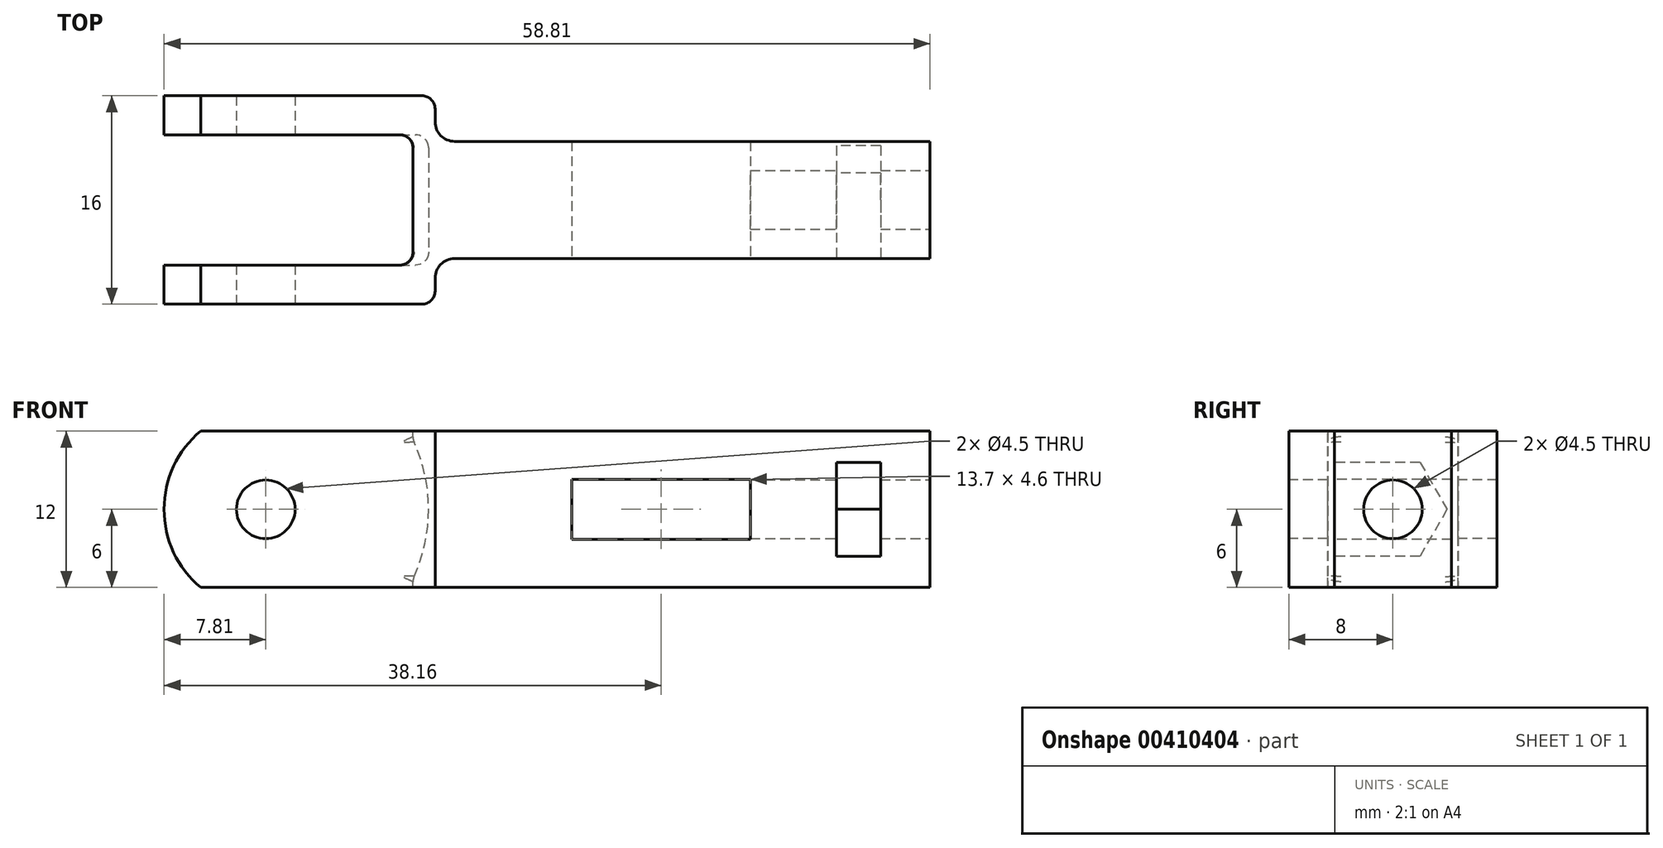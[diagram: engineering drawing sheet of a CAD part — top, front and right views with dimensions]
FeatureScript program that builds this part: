
annotation { "Feature Type Name" : "Feature", "Feature Type Description" : "" }
export const myFeature = defineFeature(function(context is Context, id is Id, definition is map)
    precondition{}
    {
        {
            var Q0;
            Q0=qCreatedBy(makeId("Top.planeOp"),FACE);
            var sketch = newSketch(context, id + "F0", { "sketchPlane" : qUnion([Q0])});
            skLineSegment(sketch, "E0", {"start": v(-5, 8) * mm, "end": v(-5, -8) * mm});
            skLineSegment(sketch, "E1", {"start": v(-5, 8) * mm, "end": v(13, 8) * mm});
            skLineSegment(sketch, "E2", {"start": v(13, 8) * mm, "end": v(13, 4.5) * mm});
            skLineSegment(sketch, "E3", {"start": v(13, 4.5) * mm, "end": v(51, 4.5) * mm});
            skLineSegment(sketch, "E4", {"start": v(51, 4.5) * mm, "end": v(51, -4.5) * mm});
            skLineSegment(sketch, "E5", {"start": v(51, -4.5) * mm, "end": v(13, -4.5) * mm});
            skLineSegment(sketch, "E6", {"start": v(13, -4.5) * mm, "end": v(13, -8) * mm});
            skLineSegment(sketch, "E7", {"start": v(13, -8) * mm, "end": v(-5, -8) * mm});
            skLineSegment(sketch, "E8", {"start": v(0, 0) * mm, "end": v(51, 0) * mm, "construction": true});
            skSolve(sketch);
        }
        {
            var Q0;
            Q0=makeQuery(id+"F0.imprint","IMPRINT",FACE,{"disambiguationData":[TD([[makeQuery(id+"F0.imprint","IMPRINT",EDGE,{"derivedFrom":sQuery(id+"F0.wireOp",EDGE,"E0")}),1.0]])]});
            extrude(context, id + "F1", {"entities" : qUnion([Q0]), "endBound" : BoundingType.SYMMETRIC, "depth" : 12 * mm});
        }
        {
            var Q0;
            Q0=makeQuery(id+"F1.opExtrude","SWEPT_FACE",FACE,{"disambiguationData":[OSD([sQuery(id+"F0.wireOp",EDGE,"E7")])]});
            var sketch = newSketch(context, id + "F2", { "sketchPlane" : qUnion([Q0])});
            skCircle(sketch, "E9", {"center": v(0, 0) * mm, "radius": 2.25 * mm});
            skSolve(sketch);
        }
        {
            var Q0;
            Q0=makeQuery(id+"F2.imprint","IMPRINT",FACE,{"disambiguationData":[TD([[makeQuery(id+"F2.imprint","IMPRINT",EDGE,{"derivedFrom":sQuery(id+"F2.wireOp",EDGE,"E9")}),1.0]])]});
            extrude(context, id + "F3", {"entities" : qUnion([Q0]), "operationType" : NewBodyOperationType.REMOVE, "endBound" : BoundingType.THROUGH_ALL, "oppositeDirection" : true, "depth" : 25 * mm});
        }
        {
            var Q0;
            Q0=makeQuery(id+"F1.opExtrude","SWEPT_FACE",FACE,{"disambiguationData":[OSD([sQuery(id+"F0.wireOp",EDGE,"E7")])]});
            var sketch = newSketch(context, id + "F4", { "sketchPlane" : qUnion([Q0])});
            skArc(sketch, "E10", {"start": v(-5, 6) * mm, "mid": v(-7.81, 0) * mm, "end": v(-5, -6) * mm});
            skLineSegment(sketch, "E11", {"start": v(-5, -6) * mm, "end": v(-5, 6) * mm});
            skSolve(sketch);
        }
        {
            var Q0;
            Q0=makeQuery(id+"F4.imprint","IMPRINT",FACE,{"disambiguationData":[TD([[makeQuery(id+"F4.imprint","IMPRINT",EDGE,{"derivedFrom":sQuery(id+"F4.wireOp",EDGE,"E10")}),1.0]])]});
            var Q1;
            Q1=makeQuery(id+"F1.opExtrude","SWEPT_FACE",FACE,{"disambiguationData":[OSD([sQuery(id+"F0.wireOp",EDGE,"E1")])]});
            extrude(context, id + "F5", {"entities" : qUnion([Q0]), "operationType" : NewBodyOperationType.ADD, "endBound" : BoundingType.UP_TO_SURFACE, "oppositeDirection" : true, "endBoundEntityFace" : qUnion([Q1]), "depth" : 25 * mm});
        }
        {
            var Q0;
            Q0=makeQuery(id+"F1.opExtrude","SWEPT_EDGE",EDGE,{"disambiguationData":[OSD([sQuery(id+"F0.wireOp",EDGE,"E2"),sQuery(id+"F0.wireOp",EDGE,"E3")])]});
            var Q1;
            Q1=makeQuery(id+"F1.opExtrude","SWEPT_EDGE",EDGE,{"disambiguationData":[OSD([sQuery(id+"F0.wireOp",EDGE,"E5"),sQuery(id+"F0.wireOp",EDGE,"E6")])]});
            fillet(context, id + "F6", {"entities" : qUnion([Q0, Q1]), "radius" : 1.5 * mm, "tangentPropagation" : true, "allowEdgeOverflow" : false});
        }
        {
            var Q0;
            Q0=qCreatedBy(makeId("Front.planeOp"),FACE);
            var sketch = newSketch(context, id + "F7", { "sketchPlane" : qUnion([Q0])});
            skArc(sketch, "E12", {"start": v(11.3, -5.34) * mm, "mid": v(12.5, 0) * mm, "end": v(11.3, 5.34) * mm});
            skLineSegment(sketch, "E13", {"start": v(11.3, 5.34) * mm, "end": v(11.3, 6) * mm});
            skLineSegment(sketch, "E14", {"start": v(-5, -6) * mm, "end": v(11.3, -6) * mm});
            skLineSegment(sketch, "E15", {"start": v(11.3, -6) * mm, "end": v(11.3, -5.34) * mm});
            skLineSegment(sketch, "E16", {"start": v(-5, 6) * mm, "end": v(11.3, 6) * mm});
            skArc(sketch, "E17.0", {"start": v(-5, 6) * mm, "mid": v(-7.81, 0) * mm, "end": v(-5, -6) * mm});
            skSolve(sketch);
        }
        {
            var Q0;
            Q0=makeQuery(id+"F7.imprint","IMPRINT",FACE,{"disambiguationData":[TD([[makeQuery(id+"F7.imprint","IMPRINT",EDGE,{"derivedFrom":sQuery(id+"F7.wireOp",EDGE,"E12")}),1.0]])]});
            extrude(context, id + "F8", {"entities" : qUnion([Q0]), "operationType" : NewBodyOperationType.REMOVE, "endBound" : BoundingType.SYMMETRIC, "oppositeDirection" : true, "depth" : 10 * mm});
        }
        {
            var Q0;
            Q0=makeQuery(id+"F1.opExtrude","SWEPT_FACE",FACE,{"disambiguationData":[OSD([sQuery(id+"F0.wireOp",EDGE,"E5")])]});
            var sketch = newSketch(context, id + "F9", { "sketchPlane" : qUnion([Q0])});
            skLineSegment(sketch, "E18", {"start": v(51, 0) * mm, "end": v(30.35, 0) * mm, "construction": true});
            skLineSegment(sketch, "E19.rect.bottom", {"start": v(37.2, 2.3) * mm, "end": v(23.5, 2.3) * mm});
            skLineSegment(sketch, "E19.rect.top", {"start": v(37.2, -2.3) * mm, "end": v(23.5, -2.3) * mm});
            skLineSegment(sketch, "E19.rect.left", {"start": v(37.2, 2.3) * mm, "end": v(37.2, -2.3) * mm});
            skLineSegment(sketch, "E19.rect.right", {"start": v(23.5, 2.3) * mm, "end": v(23.5, -2.3) * mm});
            skPoint(sketch, "E19.rect.middle", {"position": v(30.35, 0) * mm});
            skSolve(sketch);
        }
        {
            var Q0;
            Q0=makeQuery(id+"F9.imprint","IMPRINT",FACE,{"disambiguationData":[TD([[makeQuery(id+"F9.imprint","IMPRINT",EDGE,{"derivedFrom":sQuery(id+"F9.wireOp",EDGE,"E19.rect.bottom")}),1.0]])]});
            extrude(context, id + "F10", {"entities" : qUnion([Q0]), "operationType" : NewBodyOperationType.REMOVE, "endBound" : BoundingType.THROUGH_ALL, "oppositeDirection" : true, "depth" : 25 * mm});
        }
        {
            var Q0;
            Q0=makeQuery(id+"F1.opExtrude","SWEPT_FACE",FACE,{"disambiguationData":[OSD([sQuery(id+"F0.wireOp",EDGE,"E5")])]});
            var sketch = newSketch(context, id + "F11", { "sketchPlane" : qUnion([Q0])});
            skLineSegment(sketch, "E20", {"start": v(51, 0) * mm, "end": v(45.5, 0) * mm, "construction": true});
            skLineSegment(sketch, "E21.rect.bottom", {"start": v(47.2, 3.6) * mm, "end": v(43.8, 3.6) * mm});
            skLineSegment(sketch, "E21.rect.top", {"start": v(47.2, -3.6) * mm, "end": v(43.8, -3.6) * mm});
            skLineSegment(sketch, "E21.rect.left", {"start": v(47.2, 3.6) * mm, "end": v(47.2, -3.6) * mm});
            skLineSegment(sketch, "E21.rect.right", {"start": v(43.8, 3.6) * mm, "end": v(43.8, -3.6) * mm});
            skPoint(sketch, "E21.rect.middle", {"position": v(45.5, 0) * mm});
            skSolve(sketch);
        }
        {
            var Q0;
            Q0=makeQuery(id+"F11.imprint","IMPRINT",FACE,{"disambiguationData":[TD([[makeQuery(id+"F11.imprint","IMPRINT",EDGE,{"derivedFrom":sQuery(id+"F11.wireOp",EDGE,"E21.rect.bottom")}),1.0]])]});
            extrude(context, id + "F12", {"entities" : qUnion([Q0]), "operationType" : NewBodyOperationType.REMOVE, "endBound" : BoundingType.THROUGH_ALL, "oppositeDirection" : true, "depth" : 25 * mm});
        }
        {
            var Q0;
            Q0=makeQuery(id+"F1.opExtrude","SWEPT_FACE",FACE,{"disambiguationData":[OSD([sQuery(id+"F0.wireOp",EDGE,"E4")])]});
            var sketch = newSketch(context, id + "F13", { "sketchPlane" : qUnion([Q0])});
            skCircle(sketch, "E22", {"center": v(0, 0) * mm, "radius": 2.25 * mm});
            skSolve(sketch);
        }
        {
            var Q0;
            Q0=makeQuery(id+"F13.imprint","IMPRINT",FACE,{"disambiguationData":[TD([[makeQuery(id+"F13.imprint","IMPRINT",EDGE,{"derivedFrom":sQuery(id+"F13.wireOp",EDGE,"E22")}),1.0]])]});
            var Q1;
            Q1=makeQuery(id+"F10.boolean.opBoolean","COPY",FACE,{"derivedFrom":makeQuery(id+"F10.opExtrude","SWEPT_FACE",FACE,{"disambiguationData":[OSD([sQuery(id+"F9.wireOp",EDGE,"E19.rect.left")])]})});
            extrude(context, id + "F14", {"entities" : qUnion([Q0]), "operationType" : NewBodyOperationType.REMOVE, "endBound" : BoundingType.UP_TO_SURFACE, "oppositeDirection" : true, "endBoundEntityFace" : qUnion([Q1]), "depth" : 25 * mm});
        }
        {
            var Q0;
            Q0=makeQuery(id+"F12.boolean.opBoolean","COPY",FACE,{"derivedFrom":makeQuery(id+"F12.opExtrude","SWEPT_FACE",FACE,{"disambiguationData":[OSD([sQuery(id+"F11.wireOp",EDGE,"E21.rect.right")])]})});
            var sketch = newSketch(context, id + "F15", { "sketchPlane" : qUnion([Q0])});
            skCircle(sketch, "E23.cCircle", {"center": v(0, 0) * mm, "radius": 3.6 * mm, "construction": true});
            skLineSegment(sketch, "E23.0", {"start": v(-2.08, 3.6) * mm, "end": v(2.08, 3.6) * mm, "construction": true});
            skLineSegment(sketch, "E23.1", {"start": v(2.08, 3.6) * mm, "end": v(4.16, 0) * mm});
            skLineSegment(sketch, "E23.2", {"start": v(4.16, 0) * mm, "end": v(2.08, -3.6) * mm});
            skLineSegment(sketch, "E23.3", {"start": v(2.08, -3.6) * mm, "end": v(-2.08, -3.6) * mm, "construction": true});
            skLineSegment(sketch, "E23.4", {"start": v(-2.08, -3.6) * mm, "end": v(-4.16, 0) * mm, "construction": true});
            skLineSegment(sketch, "E23.5", {"start": v(-4.16, 0) * mm, "end": v(-2.08, 3.6) * mm, "construction": true});
            skPoint(sketch, "E23.0.midPoint", {"position": v(0, 3.6) * mm});
            skSolve(sketch);
        }
        {
            var Q0;
            Q0=qSketchRegion(id+"F15",true);
            var Q1;
            {var subQ5=sQuery(id+"F15.wireOp",EDGE,"E23.1");Q1=makeQuery(id+"F15.imprint","IMPRINT",FACE,{"disambiguationData":[TD([[makeQuery(id+"F15.imprint","IMPRINT",EDGE,{"derivedFrom":subQ5}),1.0]])]});}
            var Q2;
            {var subQ5=sQuery(id+"F15.wireOp",EDGE,"E23.1");Q2=makeQuery(id+"F15.imprint","IMPRINT",FACE,{"disambiguationData":[TD([[makeQuery(id+"F15.imprint","IMPRINT",EDGE,{"derivedFrom":subQ5}),1.0]])]});}
            var Q3;
            Q3=makeQuery(id+"F12.boolean.opBoolean","COPY",FACE,{"derivedFrom":makeQuery(id+"F12.opExtrude","SWEPT_FACE",FACE,{"disambiguationData":[OSD([sQuery(id+"F11.wireOp",EDGE,"E21.rect.left")])]})});
            extrude(context, id + "F16", {"entities" : qUnion([Q0, Q1, Q2]), "operationType" : NewBodyOperationType.ADD, "endBound" : BoundingType.UP_TO_SURFACE, "endBoundEntityFace" : qUnion([Q3]), "depth" : 25 * mm});
        }
        {
            var Q0;
            Q0=makeQuery(id+"F8.boolean.opBoolean","COPY",EDGE,{"derivedFrom":makeQuery(id+"F8.opExtrude","CAP_EDGE",EDGE,{"disambiguationData":[OSD([sQuery(id+"F7.wireOp",EDGE,"E12")])],"isStart":false})});
            var Q1;
            Q1=makeQuery(id+"F8.boolean.opBoolean","COPY",EDGE,{"derivedFrom":makeQuery(id+"F8.opExtrude","CAP_EDGE",EDGE,{"disambiguationData":[OSD([sQuery(id+"F7.wireOp",EDGE,"E13")])],"isStart":false})});
            var Q2;
            Q2=makeQuery(id+"F8.boolean.opBoolean","COPY",EDGE,{"derivedFrom":makeQuery(id+"F8.opExtrude","CAP_EDGE",EDGE,{"disambiguationData":[OSD([sQuery(id+"F7.wireOp",EDGE,"E15")])],"isStart":false})});
            var Q3;
            Q3=makeQuery(id+"F8.boolean.opBoolean","COPY",EDGE,{"derivedFrom":makeQuery(id+"F8.opExtrude","CAP_EDGE",EDGE,{"disambiguationData":[OSD([sQuery(id+"F7.wireOp",EDGE,"E15")])],"isStart":true})});
            var Q4;
            Q4=makeQuery(id+"F8.boolean.opBoolean","COPY",EDGE,{"derivedFrom":makeQuery(id+"F8.opExtrude","CAP_EDGE",EDGE,{"disambiguationData":[OSD([sQuery(id+"F7.wireOp",EDGE,"E12")])],"isStart":true})});
            var Q5;
            Q5=makeQuery(id+"F8.boolean.opBoolean","COPY",EDGE,{"derivedFrom":makeQuery(id+"F8.opExtrude","CAP_EDGE",EDGE,{"disambiguationData":[OSD([sQuery(id+"F7.wireOp",EDGE,"E13")])],"isStart":true})});
            fillet(context, id + "F17", {"entities" : qUnion([Q0, Q1, Q2, Q3, Q4, Q5]), "radius" : 1 * mm, "tangentPropagation" : true, "allowEdgeOverflow" : false});
        }
        {
            var Q0;
            Q0=makeQuery(id+"F17.opFillet","BLEND_EDGE",EDGE,{"blendedFrom":[makeQuery(id+"F8.boolean.opBoolean","COPY",EDGE,{"derivedFrom":makeQuery(id+"F8.opExtrude","CAP_EDGE",EDGE,{"disambiguationData":[OSD([sQuery(id+"F7.wireOp",EDGE,"E12")])],"isStart":false})}),makeQuery(id+"F8.boolean.opBoolean","COPY",EDGE,{"derivedFrom":makeQuery(id+"F8.opExtrude","CAP_EDGE",EDGE,{"disambiguationData":[OSD([sQuery(id+"F7.wireOp",EDGE,"E15")])],"isStart":false})})],"blendedInto":[]});
            var Q1;
            Q1=makeQuery(id+"F8.boolean.opBoolean","COPY",EDGE,{"derivedFrom":makeQuery(id+"F8.opExtrude","SWEPT_EDGE",EDGE,{"disambiguationData":[OSD([sQuery(id+"F7.wireOp",EDGE,"E12"),sQuery(id+"F7.wireOp",EDGE,"E15")])]})});
            var Q2;
            Q2=makeQuery(id+"F17.opFillet","BLEND_EDGE",EDGE,{"blendedFrom":[makeQuery(id+"F8.boolean.opBoolean","COPY",EDGE,{"derivedFrom":makeQuery(id+"F8.opExtrude","CAP_EDGE",EDGE,{"disambiguationData":[OSD([sQuery(id+"F7.wireOp",EDGE,"E12")])],"isStart":true})}),makeQuery(id+"F8.boolean.opBoolean","COPY",EDGE,{"derivedFrom":makeQuery(id+"F8.opExtrude","CAP_EDGE",EDGE,{"disambiguationData":[OSD([sQuery(id+"F7.wireOp",EDGE,"E15")])],"isStart":true})})],"blendedInto":[]});
            var Q3;
            Q3=makeQuery(id+"F17.opFillet","BLEND_EDGE",EDGE,{"blendedFrom":[makeQuery(id+"F8.boolean.opBoolean","COPY",EDGE,{"derivedFrom":makeQuery(id+"F8.opExtrude","CAP_EDGE",EDGE,{"disambiguationData":[OSD([sQuery(id+"F7.wireOp",EDGE,"E12")])],"isStart":true})}),makeQuery(id+"F8.boolean.opBoolean","COPY",EDGE,{"derivedFrom":makeQuery(id+"F8.opExtrude","CAP_EDGE",EDGE,{"disambiguationData":[OSD([sQuery(id+"F7.wireOp",EDGE,"E13")])],"isStart":true})})],"blendedInto":[]});
            var Q4;
            Q4=makeQuery(id+"F8.boolean.opBoolean","COPY",EDGE,{"derivedFrom":makeQuery(id+"F8.opExtrude","SWEPT_EDGE",EDGE,{"disambiguationData":[OSD([sQuery(id+"F7.wireOp",EDGE,"E12"),sQuery(id+"F7.wireOp",EDGE,"E13")])]})});
            var Q5;
            Q5=makeQuery(id+"F17.opFillet","BLEND_EDGE",EDGE,{"blendedFrom":[makeQuery(id+"F8.boolean.opBoolean","COPY",EDGE,{"derivedFrom":makeQuery(id+"F8.opExtrude","CAP_EDGE",EDGE,{"disambiguationData":[OSD([sQuery(id+"F7.wireOp",EDGE,"E12")])],"isStart":false})}),makeQuery(id+"F8.boolean.opBoolean","COPY",EDGE,{"derivedFrom":makeQuery(id+"F8.opExtrude","CAP_EDGE",EDGE,{"disambiguationData":[OSD([sQuery(id+"F7.wireOp",EDGE,"E13")])],"isStart":false})})],"blendedInto":[]});
            fillet(context, id + "F18", {"entities" : qUnion([Q0, Q1, Q2, Q3, Q4, Q5]), "radius" : 1 * mm, "tangentPropagation" : true, "allowEdgeOverflow" : false});
        }
        {
            var Q0;
            Q0=makeQuery(id+"F1.opExtrude","SWEPT_EDGE",EDGE,{"disambiguationData":[OSD([sQuery(id+"F0.wireOp",EDGE,"E1"),sQuery(id+"F0.wireOp",EDGE,"E2")])]});
            var Q1;
            Q1=makeQuery(id+"F1.opExtrude","SWEPT_EDGE",EDGE,{"disambiguationData":[OSD([sQuery(id+"F0.wireOp",EDGE,"E6"),sQuery(id+"F0.wireOp",EDGE,"E7")])]});
            fillet(context, id + "F19", {"entities" : qUnion([Q0, Q1]), "radius" : 1 * mm, "tangentPropagation" : true, "allowEdgeOverflow" : false});
        }
    });
